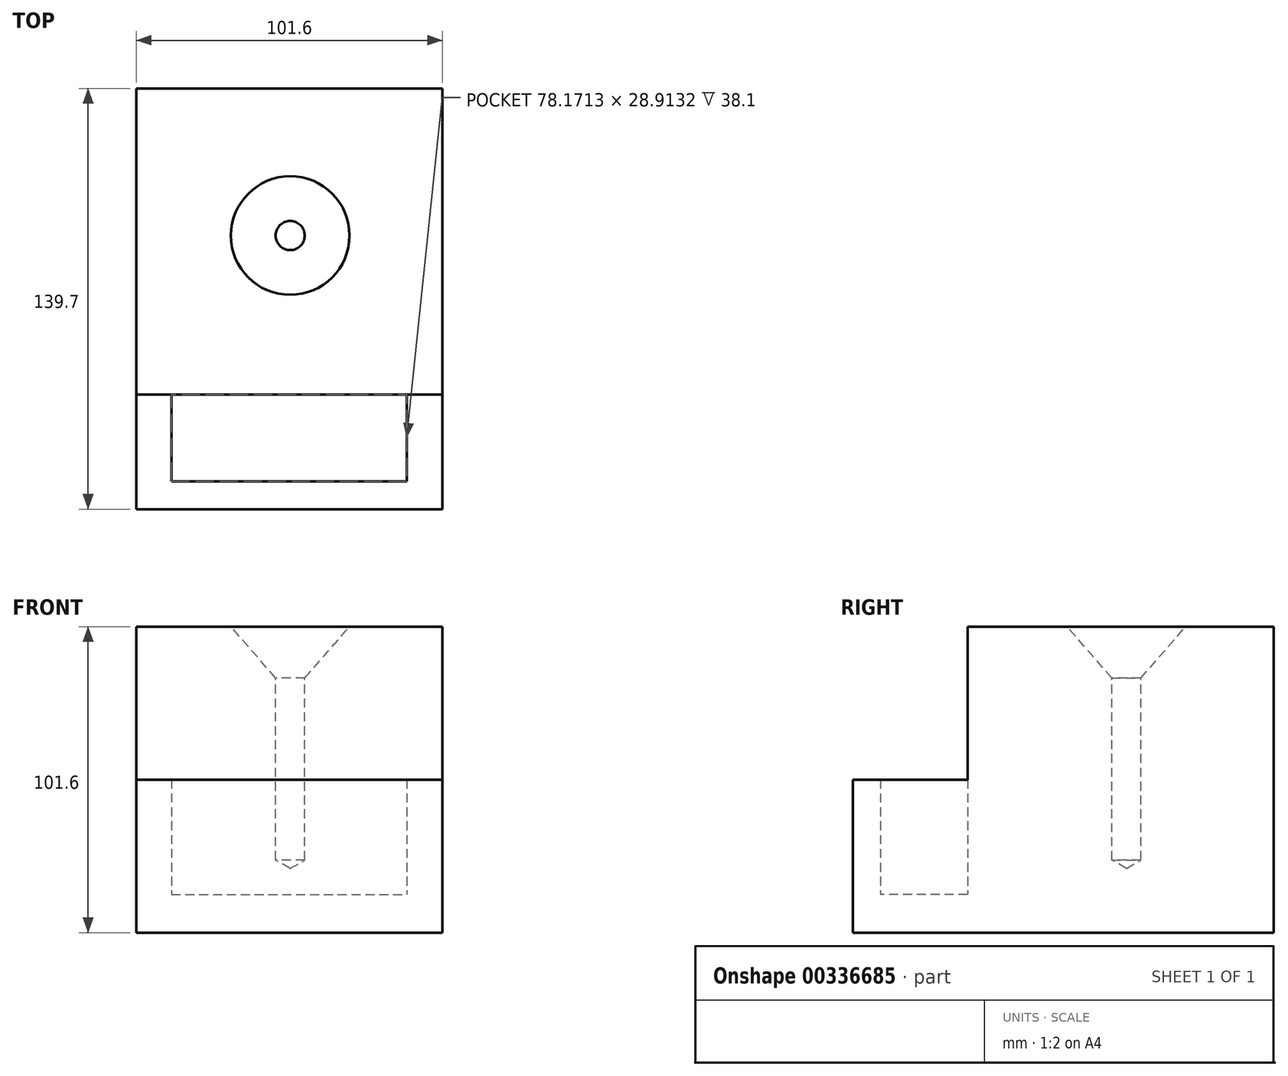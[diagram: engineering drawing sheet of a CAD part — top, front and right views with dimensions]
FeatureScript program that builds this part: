
annotation { "Feature Type Name" : "Feature", "Feature Type Description" : "" }
export const myFeature = defineFeature(function(context is Context, id is Id, definition is map)
    precondition{}
    {
        {
            var Q0;
            Q0=qCreatedBy(makeId("Top.planeOp"),FACE);
            var sketch = newSketch(context, id + "F0", { "sketchPlane" : qUnion([Q0])});
            skLineSegment(sketch, "E0.bottom", {"start": v(-51.1, 48.87) * mm, "end": v(50.5, 48.87) * mm});
            skLineSegment(sketch, "E0.top", {"start": v(-51.1, -52.73) * mm, "end": v(50.5, -52.73) * mm});
            skLineSegment(sketch, "E0.left", {"start": v(-51.1, 48.87) * mm, "end": v(-51.1, -52.73) * mm});
            skLineSegment(sketch, "E0.right", {"start": v(50.5, 48.87) * mm, "end": v(50.5, -52.73) * mm});
            skSolve(sketch);
        }
        {
            var Q0;
            Q0=qSketchRegion(id+"F0",true);
            extrude(context, id + "F1", {"entities" : qUnion([Q0]), "depth" : 101.6 * mm});
        }
        {
            var Q0;
            Q0=makeQuery(id+"F1.opExtrude","CAP_FACE",FACE,{"disambiguationData":[OSD([sQuery(id+"F0.wireOp",EDGE,"E0.bottom"),sQuery(id+"F0.wireOp",EDGE,"E0.top"),sQuery(id+"F0.wireOp",EDGE,"E0.left"),sQuery(id+"F0.wireOp",EDGE,"E0.right")])],"isStart":false});
            var sketch = newSketch(context, id + "F2", { "sketchPlane" : qUnion([Q0])});
            skCircle(sketch, "E1", {"center": v(0, 0) * mm, "radius": 20.44 * mm});
            skSolve(sketch);
        }
        {
            var Q0;
            Q0=sQuery(id+"F2.wireOp",VERTEX,"E1.center");
            var Q1;
            Q1=makeQuery(id+"F1.opExtrude","SWEPT_BODY",BODY,{"disambiguationData":[OSD([sQuery(id+"F0.wireOp",EDGE,"E0.bottom"),sQuery(id+"F0.wireOp",EDGE,"E0.top"),sQuery(id+"F0.wireOp",EDGE,"E0.left"),sQuery(id+"F0.wireOp",EDGE,"E0.right")])]});
            hole(context, id + "F3", {"style" : HoleStyle.C_SINK, "endStyle" : HoleEndStyle.BLIND, "holeDiameter" : 9.65 * mm, "cSinkDiameter" : 39.37 * mm, "cSinkAngle" : 82 * degree, "holeDepth" : 77.47 * mm, "tappedDepth" : 12.7 * mm, "tapClearance" : 3, "startFromSketch" : true, "locations" : qUnion([Q0]), "scope" : qUnion([Q1])});
        }
        {
            var Q0;
            Q0=makeQuery(id+"F1.opExtrude","SWEPT_FACE",FACE,{"disambiguationData":[OSD([sQuery(id+"F0.wireOp",EDGE,"E0.top")])]});
            var sketch = newSketch(context, id + "F4", { "sketchPlane" : qUnion([Q0])});
            skLineSegment(sketch, "E2.bottom", {"start": v(-51.1, 12.7) * mm, "end": v(50.5, 12.7) * mm});
            skLineSegment(sketch, "E2.top", {"start": v(-51.1, 0) * mm, "end": v(50.5, 0) * mm});
            skLineSegment(sketch, "E2.left", {"start": v(-51.1, 12.7) * mm, "end": v(-51.1, 0) * mm});
            skLineSegment(sketch, "E2.right", {"start": v(50.5, 12.7) * mm, "end": v(50.5, 0) * mm});
            skSolve(sketch);
        }
        {
            var Q0;
            Q0=qSketchRegion(id+"F4",true);
            extrude(context, id + "F5", {"entities" : qUnion([Q0]), "operationType" : NewBodyOperationType.ADD, "depth" : 38.1 * mm});
        }
        {
            var Q0;
            Q0=makeQuery(id+"F5.opExtrude","SWEPT_FACE",FACE,{"disambiguationData":[OSD([sQuery(id+"F4.wireOp",EDGE,"E2.bottom")])]});
            var sketch = newSketch(context, id + "F6", { "sketchPlane" : qUnion([Q0])});
            skLineSegment(sketch, "E3.bottom", {"start": v(-51.1, -52.73) * mm, "end": v(-39.42, -52.73) * mm});
            skLineSegment(sketch, "E3.top", {"start": v(-51.1, -90.83) * mm, "end": v(-39.42, -90.83) * mm});
            skLineSegment(sketch, "E3.left", {"start": v(-51.1, -52.73) * mm, "end": v(-51.1, -90.83) * mm});
            skLineSegment(sketch, "E3.right", {"start": v(-39.42, -52.73) * mm, "end": v(-39.42, -90.83) * mm});
            skLineSegment(sketch, "E4.bottom", {"start": v(50.5, -52.73) * mm, "end": v(38.75, -52.73) * mm});
            skLineSegment(sketch, "E4.top", {"start": v(50.5, -90.83) * mm, "end": v(38.75, -90.83) * mm});
            skLineSegment(sketch, "E4.left", {"start": v(50.5, -52.73) * mm, "end": v(50.5, -90.83) * mm});
            skLineSegment(sketch, "E4.right", {"start": v(38.75, -52.73) * mm, "end": v(38.75, -90.83) * mm});
            skLineSegment(sketch, "E5.bottom", {"start": v(-39.42, -81.65) * mm, "end": v(38.75, -81.65) * mm});
            skLineSegment(sketch, "E5.top", {"start": v(-39.42, -90.83) * mm, "end": v(38.75, -90.83) * mm});
            skLineSegment(sketch, "E5.left", {"start": v(-39.42, -81.65) * mm, "end": v(-39.42, -90.83) * mm});
            skLineSegment(sketch, "E5.right", {"start": v(38.75, -81.65) * mm, "end": v(38.75, -90.83) * mm});
            skSolve(sketch);
        }
        {
            var Q0;
            Q0=qSketchRegion(id+"F6",true);
            extrude(context, id + "F7", {"entities" : qUnion([Q0]), "operationType" : NewBodyOperationType.ADD, "depth" : 38.1 * mm});
        }
    });
